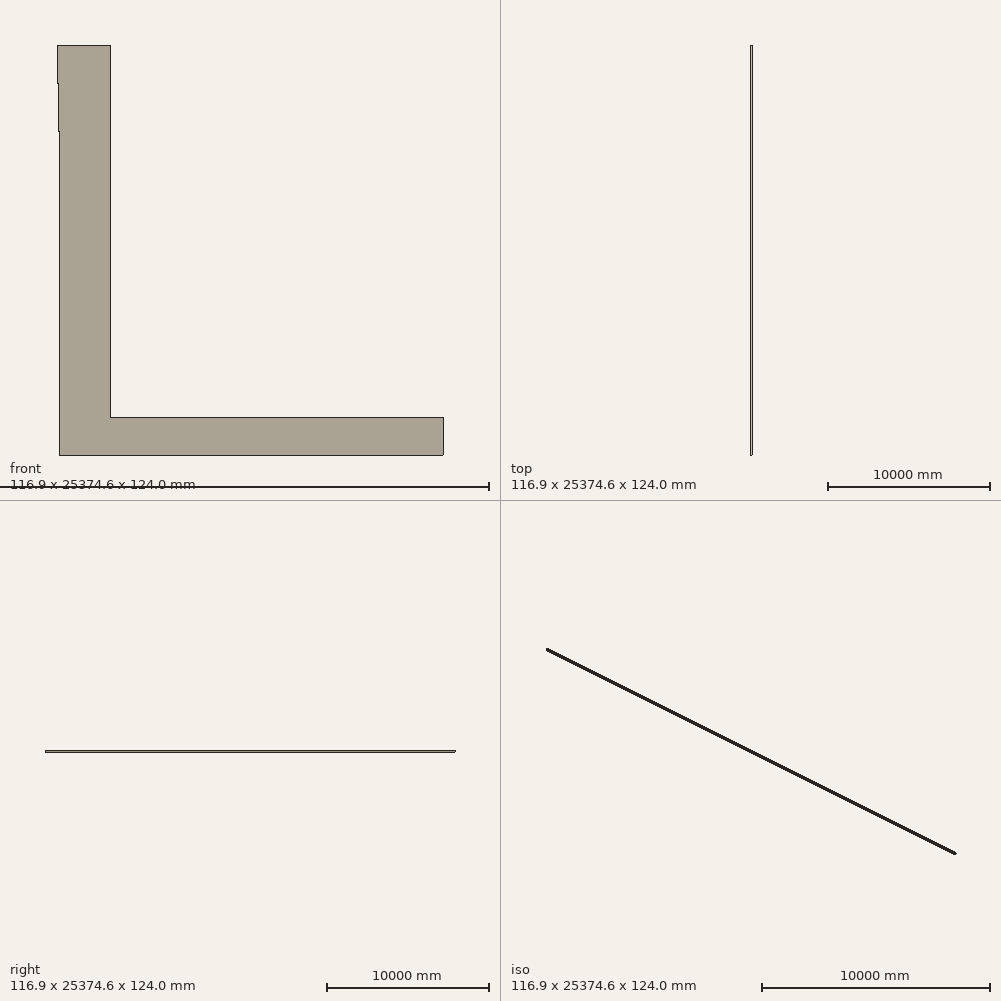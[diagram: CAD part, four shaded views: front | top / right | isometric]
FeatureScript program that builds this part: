
annotation { "Feature Type Name" : "Feature", "Feature Type Description" : "" }
export const myFeature = defineFeature(function(context is Context, id is Id, definition is map)
    precondition{}
    {
        {
            var Q0;
            Q0=qCreatedBy(makeId("Front.planeOp"),FACE);
            var sketch = newSketch(context, id + "F0", { "sketchPlane" : qUnion([Q0])});
            skLineSegment(sketch, "E0", {"start": v(-58.87, 42.7) * mm, "end": v(-58.87, -53.77) * mm});
            skLineSegment(sketch, "E1", {"start": v(-58.87, -53.77) * mm, "end": v(57.45, -53.77) * mm});
            skLineSegment(sketch, "E2", {"start": v(57.45, -53.77) * mm, "end": v(57.45, -42.13) * mm});
            skLineSegment(sketch, "E3", {"start": v(57.45, -42.13) * mm, "end": v(-43.27, -42.13) * mm});
            skLineSegment(sketch, "E4", {"start": v(-43.27, -42.13) * mm, "end": v(-43.27, 70.22) * mm});
            skLineSegment(sketch, "E5", {"start": v(-43.27, 70.22) * mm, "end": v(-59.44, 70.22) * mm});
            skLineSegment(sketch, "E6", {"start": v(-59.44, 70.22) * mm, "end": v(-58.87, 42.7) * mm});
            skSolve(sketch);
        }
        {
            var Q0;
            Q0=makeQuery(id+"F0.imprint","IMPRINT",FACE,{"disambiguationData":[TD([[makeQuery(id+"F0.imprint","IMPRINT",EDGE,{"derivedFrom":sQuery(id+"F0.wireOp",EDGE,"E0")}),1.0]])]});
            extrude(context, id + "F1", {"entities" : qUnion([Q0]), "depth" : 25374.6 * mm, "offsetDistance" : 25.4 * mm});
        }
    });
